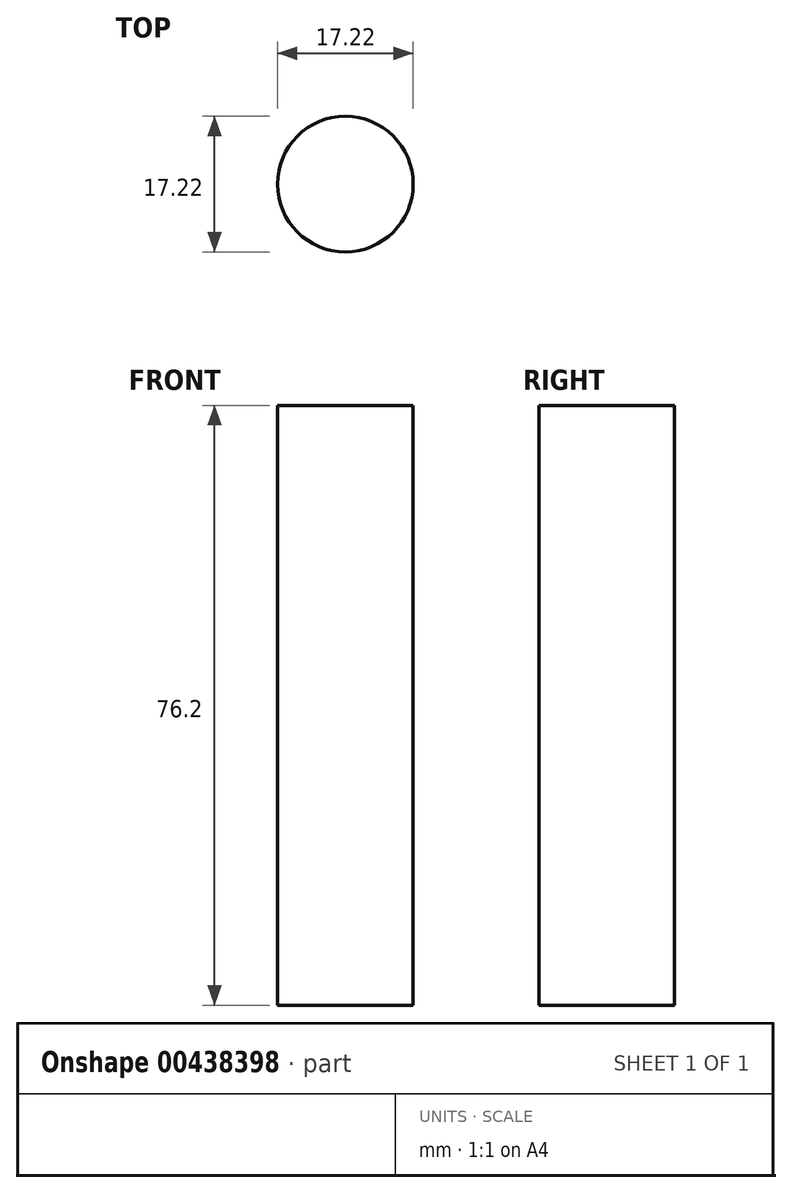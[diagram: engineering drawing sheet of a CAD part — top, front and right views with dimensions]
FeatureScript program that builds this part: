
annotation { "Feature Type Name" : "Feature", "Feature Type Description" : "" }
export const myFeature = defineFeature(function(context is Context, id is Id, definition is map)
    precondition{}
    {
        {
            var Q0;
            Q0=qCreatedBy(makeId("Top.planeOp"),FACE);
            var sketch = newSketch(context, id + "F0", { "sketchPlane" : qUnion([Q0])});
            skCircle(sketch, "E0", {"center": v(0, 0) * mm, "radius": 8.61 * mm});
            skSolve(sketch);
        }
        {
            var Q0;
            Q0=makeQuery(id+"F0.imprint","IMPRINT",FACE,{"disambiguationData":[TD([[makeQuery(id+"F0.imprint","IMPRINT",EDGE,{"derivedFrom":sQuery(id+"F0.wireOp",EDGE,"E0")}),1.0]])]});
            var Q1;
            Q1=sQuery(id+"F0.wireOp",EDGE,"E0");
            extrude(context, id + "F1", {"entities" : qUnion([Q0]), "surfaceEntities" : qUnion([Q1]), "depth" : 76.2 * mm});
        }
    });
